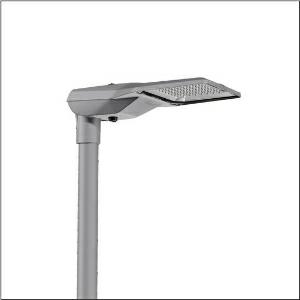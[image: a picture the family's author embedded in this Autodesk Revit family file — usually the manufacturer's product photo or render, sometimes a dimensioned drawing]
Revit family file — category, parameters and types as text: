
# Revit family: streetlight_sl_21_iq_midi___st0_5a_5xe3b31y08mb_2f18
name_source: partatom
category: Lighting Fixtures
units: mm (PartAtom-declared; Revit-internal decimal feet)

## family parameters
Cut with Voids When Loaded = No
Host = Face
Light Source = No
Part Type = Normal
Room Calculation Point = No
Round Connector Dimension = Use Diameter
Shared = No

## types (1)
- --- (1 x LED, 18340 lm, 129.3 W, 3000K)
    Apparent Load = 129 VA
    CIE Flux Codes = 41 75 97 100 100
    Color Rendering = 70
    Color Temperature = 3000K
    Default Elevation = 1800 mm
    Description = Streetlight SL 21 iQ midi, mast luminaire, primary light control with lens, of PMMA, primary optical cover: cover, of toughened safety glass, transparent, light distribution: ST0.5a, light emission: direct distribution, primary light characteristic: asymmetric, installation type: post-top, side-entry, LED, High Power LED, rated luminous flux: 18.340lm, luminous efficacy: 142lm/W, light colour: 730, colour temperature: 3000K, control gear: iQ-Street Remote, D4i with power reduction, control: pre-setting: logarithmic dimming characteristic, Street-Remote, Auto-Match, Temp-Guard, Lumen-Switch, Night-Set, Smart-Wire, Light-Fading, Desk-Remote (wireless, voltage-free reading and setting of iQ features in the workshop via application-optimized NFC function/RFID function), optimised constant luminous flux control (CLO 2.0), mains connection: 230..240V, AC, 50/60Hz, start of lifetime: 129W, end of service life: 142W, reduction: 56W, luminaire housing, of diecast aluminium, powder-coated, Siteco® metallic grey (DB 702S), corrosivity category C5 mid according to DIN EN ISO 12944, please order mast flange separately, inclination adjustable: 0°, 5°, 10°, 15°, sealing non-destructively replaceable, multi-level sealing system, length: 644mm, width: 335mm, height: 110mm, mast flange for spigot size: 42mm (side-entry): 5XC10008XM4, 60/48mm (side-entry/post-top): 5XC10108XM2, 76/60mm (side-entry/post-top): 5XC10108XM1, mounting height: 4..8m, Smart Interface below and above, protection rating (complete): IP66, insulation class (complete): insulation class II (safety insulation), certification: CE, ENEC, ENEC+, VDE, impact resistance: IK10, permissible operating ambient temperature for outdoor applications: -40..+50°C, standard-compliant lighting for roads and squares, packaging unit: 1 piece

Light Distribution: ST0.5a
    Height = 111 mm
    Lamp = 1 x LED
    Lamp Light Flux = 18340 lm
    Lamp Power = 129.3 W
    Lamp count = 1
    Length = 644 mm
    Luminous efficacy = 142 lm/W
    Manufacturer = Siteco
    ModVariant = No
    Model = 5XE3B31Y08MB
    Number of Poles = 1
    OnlyDefault = Yes
    Power Factor = 1
    Product Name = Streetlight SL 21 iQ midi | ST0.5a
    Product group = mast luminaire | pylon top
    ProductGroupID = 6100
    Protection Class = Protection class II
    Protection Degree = IP 66
    RLX_Detail_Level = 1
    RLX_Emergency_Light_Flux = 0 lm
    RLX_Emergency_Type = 0
    RLX_Emergency_Type_DB = No
    RlxData = <blob elided: 102125 chars, md5=4a021aa6>
    Socket = socket
    Standby Power = 0 W
    System Light Flux = 18340 lm
    System Power = 129 W
    Type Comments = factory setting: luminous flux: 100 % | dim-lin: 254 | 672 mA
    Type Image = l_1004304.jpg
    URL = http://relux.com
    VarID = @adj_137543
    Voltage = 0 V
    Weight = 0.00 kg
    Width = 336 mm

## geometry (parser evidence)
native form markers: Blend x4, Sweep x10
no freeform markers — native parametric forms only
